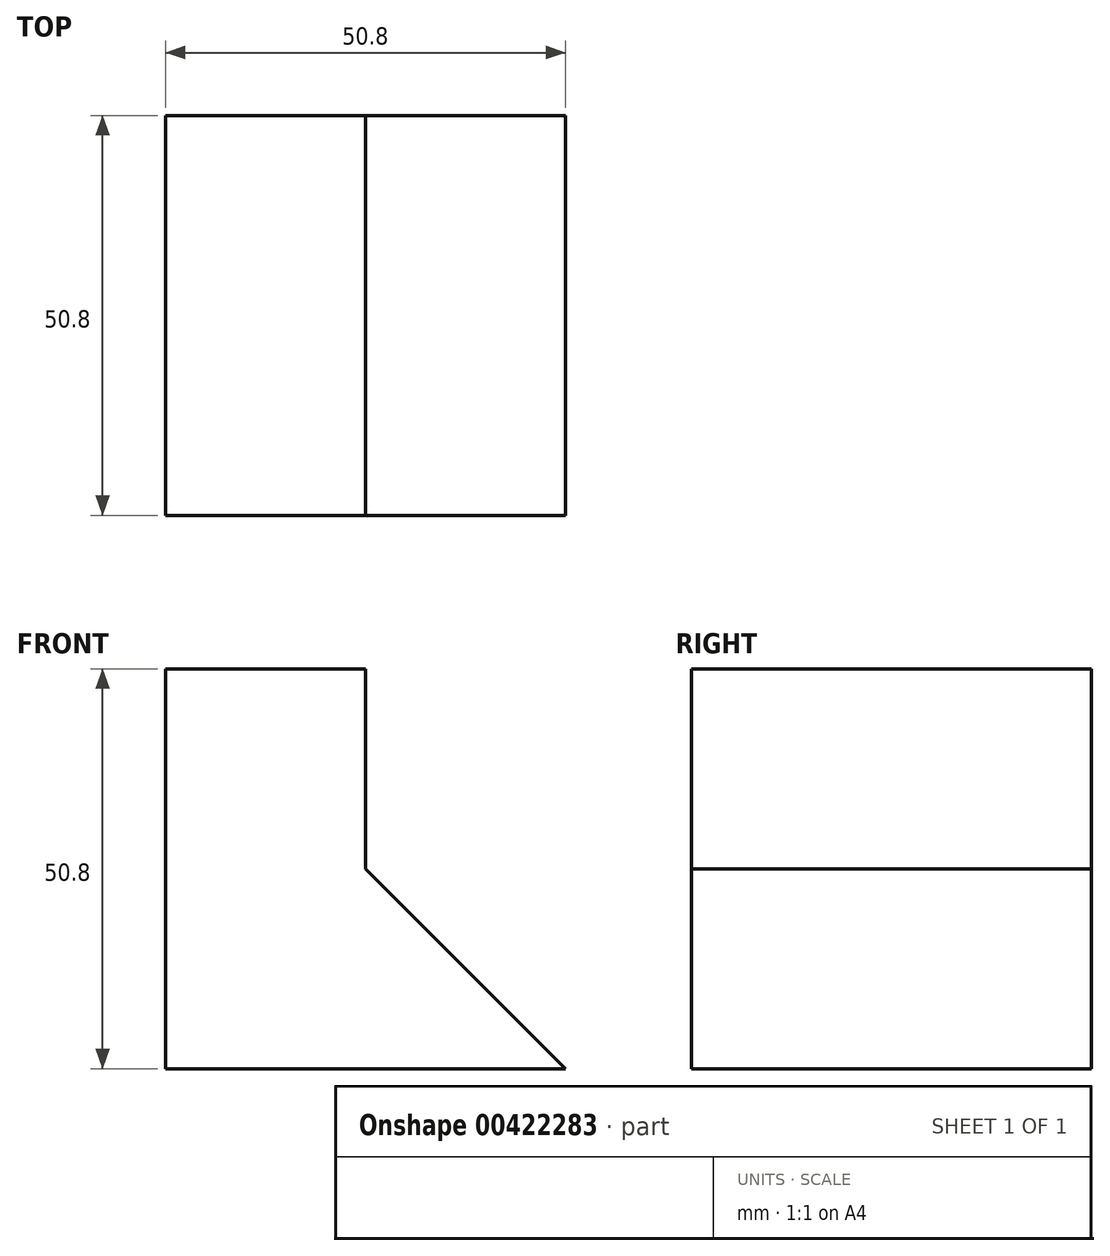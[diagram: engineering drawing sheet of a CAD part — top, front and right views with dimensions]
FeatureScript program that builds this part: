
annotation { "Feature Type Name" : "Feature", "Feature Type Description" : "" }
export const myFeature = defineFeature(function(context is Context, id is Id, definition is map)
    precondition{}
    {
        {
            var Q0;
            Q0=qCreatedBy(makeId("Front.planeOp"),FACE);
            var sketch = newSketch(context, id + "F0", { "sketchPlane" : qUnion([Q0])});
            skLineSegment(sketch, "E0", {"start": v(-64.33, 50.8) * mm, "end": v(-64.33, 0) * mm});
            skLineSegment(sketch, "E1", {"start": v(-64.33, 0) * mm, "end": v(-13.53, 0) * mm});
            skLineSegment(sketch, "E2", {"start": v(-64.33, 50.8) * mm, "end": v(-38.93, 50.8) * mm});
            skLineSegment(sketch, "E3", {"start": v(-38.93, 50.8) * mm, "end": v(-38.93, 25.4) * mm});
            skLineSegment(sketch, "E4", {"start": v(-38.93, 25.4) * mm, "end": v(-13.53, 0) * mm});
            skSolve(sketch);
        }
        {
            var Q0;
            Q0 = qSketchRegion(id + "F0", true);
            extrude(context, id + "F1", {"entities" : qUnion([Q0]), "depth" : 50.8 * mm});
        }
    });
